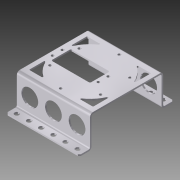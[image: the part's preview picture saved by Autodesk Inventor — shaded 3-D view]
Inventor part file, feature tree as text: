
AUTODESK INVENTOR PART (.ipt)
format: ipt  version: 2016 SP1 (Build 200210100, 210)  size: 432,640 bytes
history: native  units: in
note: dims shown in document units (in); Inventor stores cm internally (conversion verified against a paired STEP export)
features: sketch x9, other x7, extrude x4, sheet_metal_op x4, reference x4, projected_geometry x2, pattern_linear x1
ambient origin geometry x8: Origin, YZ Plane, XZ Plane, XY Plane, X Axis, Y Axis, Z Axis, Center Point
bodies: Solid1 (feature_tree)
feature tree (31):
  extrude  "Extrusion1"  Depth=2.875in
  extrude  "Extrusion2"  Depth=0.0625in
  sheet_metal_op  "Bend1"
  sheet_metal_op  "Bend2"
  extrude  "Extrusion3"  Depth=1.1875in TaperAngle=0.0deg
  sheet_metal_op  "Bend3"
  sheet_metal_op  "Bend4"
  other  "Corner Chamfer1"
  extrude  "Extrusion6"  Depth=0.0312in
  pattern_linear  "Rectangular Pattern1"  Spacing1=0.125in  [1 undecoded]
  sketch  "Sketch1"  dims[d0=3.0in d1=2.875in]
  sketch  "Sketch2"  dims[d2=0.0625in d3=0.0in d4=0.0625in]
  sketch  "Sketch3"  dims[d5=0.0625in d6=1.1875in d7=0.0in]
  projected_geometry  "Projected Loop1"
  sketch  "Sketch4"  dims[d8=0.0625in d9=0.0312in]
  projected_geometry  "Projected Loop2"
  sketch  "Sketch6"  dims[d10=0.125in]
  sketch  "Sketch7"  dims[d11=0.0625in]
  sketch  "Sketch8"  dims[d12=0.0625in]
  reference  "Reference1"
  reference  "Reference2"
  reference  "Reference3"
  reference  "Reference4"
  sketch  "Sketch9"  dims[d13=0.0625in]
  sketch  "Sketch12"  dims[d14=0.0312in d15=0.125in d16=0.0625in d17=0.0625in d18=0.4375in d19=0.4375in d20=0.0625in d21=0.0in d22=0.0625in d23=0.0312in d24=0.125in d25=0.0625in d26=0.0625in d27=0.0625in d28=0.0312in d29=0.125in d30=0.0625in d31=0.0625in d32=0.1875in d33=0.1875in d34=0.25in d35=0.25in d36=2.3622in d38=0.5in d39=0.3937in d41=1.0in d43=0.0625in d44=0.0in d57=0.1875in d58=0.0312in d59=0.0312in d60=0.0312in d61=0.0312in d62=0.0312in d63=0.0312in d64=0.3375in d65=0.0625in d66=0.0in d67=0.4016in d68=1.8819in d69=0.113in d71=0.5829in d72=0.0625in d73=0.0in d74=0.0625in d75=0.25in d76=45.0deg d78=0.0625in d79=0.0in d80=2.4in d81=0.113in d82=2.3622in d84=360.0deg d86=0.0625in d87=0.0in d92=0.688in d93=0.656in d94=0.531in d95=1.0in d96=0.0in d97=1.1811in d99=0.969in]
  other  "Cut1"
  other  "Cut3"
  other  "Cut4"
  other  "Cut5"
  other  "Cut6"
  other  "Definition1"
note: 1 required parameter value undecoded (feature->parameter linkage not recoverable at this tier; creation-order binding heuristic only, values carry confidence <= 0.55)
